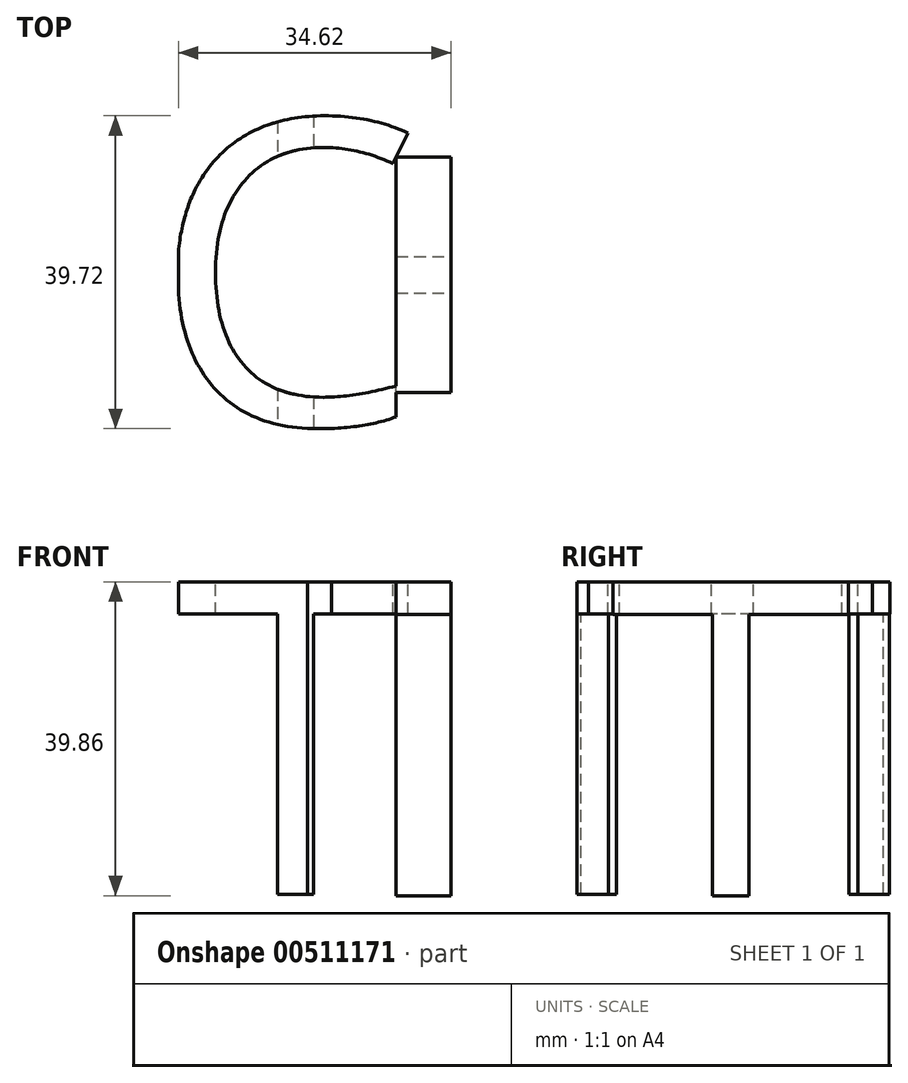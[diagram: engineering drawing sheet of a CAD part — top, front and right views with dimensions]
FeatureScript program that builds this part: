
annotation { "Feature Type Name" : "Feature", "Feature Type Description" : "" }
export const myFeature = defineFeature(function(context is Context, id is Id, definition is map)
    precondition{}
    {
        {
            var Q0;
            Q0=qCreatedBy(makeId("Top.planeOp"),FACE);
            var sketch = newSketch(context, id + "F0", { "sketchPlane" : qUnion([Q0])});
            skLineSegment(sketch, "E0.bottom", {"start": v(-20, 20) * mm, "end": v(20, 20) * mm});
            skLineSegment(sketch, "E0.top", {"start": v(-20, -20) * mm, "end": v(20, -20) * mm});
            skLineSegment(sketch, "E0.left", {"start": v(-20, 20) * mm, "end": v(-20, -20) * mm});
            skLineSegment(sketch, "E0.right", {"start": v(20, 20) * mm, "end": v(20, -20) * mm});
            skLineSegment(sketch, "E1", {"start": v(-20, 0) * mm, "end": v(20, 0) * mm, "construction": true});
            skSolve(sketch);
        }
        {
            var Q0;
            Q0 = qSketchRegion(id + "F0", true);
            extrude(context, id + "F1", {"entities" : qUnion([Q0]), "oppositeDirection" : true, "depth" : 40 * mm});
        }
        {
            var Q0;
            Q0=makeQuery(id+"F1.opExtrude","CAP_FACE",FACE,{"disambiguationData":[OSD([sQuery(id+"F0.wireOp",EDGE,"E0.bottom"),sQuery(id+"F0.wireOp",EDGE,"E0.top"),sQuery(id+"F0.wireOp",EDGE,"E0.left"),sQuery(id+"F0.wireOp",EDGE,"E0.right")])],"isStart":true});
            var sketch = newSketch(context, id + "F2", { "sketchPlane" : qUnion([Q0])});
            skText(sketch, "E2", { "text": "C\n", "fontName": "OpenSans-Regular.ttf"});
            const initialGuessF2  = {"E2": [-0.01804, -0.0195, 1, 0, 0.039]};
            skSetInitialGuess(sketch, initialGuessF2);
            skSolve(sketch);
        }
        {
            var Q0;
            Q0=makeQuery(id+"F1.opExtrude","SWEPT_FACE",FACE,{"disambiguationData":[OSD([sQuery(id+"F0.wireOp",EDGE,"E0.top")])]});
            var sketch = newSketch(context, id + "F3", { "sketchPlane" : qUnion([Q0])});
            skText(sketch, "E3", { "text": "T", "fontName": "OpenSans-Regular.ttf"});
            skLineSegment(sketch, "E4", {"start": v(-20, -20) * mm, "end": v(20, -20) * mm, "construction": true});
            const initialGuessF3  = {"E3": [-0.01511, -0.04, 1, 0, 0.04]};
            skSetInitialGuess(sketch, initialGuessF3);
            skSolve(sketch);
        }
        {
            var Q0;
            Q0=makeQuery(id+"F1.opExtrude","SWEPT_FACE",FACE,{"disambiguationData":[OSD([sQuery(id+"F0.wireOp",EDGE,"E0.right")])]});
            var sketch = newSketch(context, id + "F4", { "sketchPlane" : qUnion([Q0])});
            skText(sketch, "E5", { "text": "T", "fontName": "OpenSans-Regular.ttf"});
            skLineSegment(sketch, "E6", {"start": v(-20, -20) * mm, "end": v(20, -20) * mm, "construction": true});
            const initialGuessF4  = {"E5": [-0.0159, -0.0402, 1, 0, 0.0402]};
            skSetInitialGuess(sketch, initialGuessF4);
            skSolve(sketch);
        }
        {
            var Q0;
            Q0=makeQuery(id+"F2.imprint","IMPRINT",FACE,{"disambiguationData":[TD([[makeQuery(id+"F2.imprint","IMPRINT",EDGE,{"derivedFrom":sQuery(id+"F2.wireOp",EDGE,"E2.sketch_text.stroke-0")}),1.0]])]});
            extrude(context, id + "F5", {"entities" : qUnion([Q0]), "operationType" : NewBodyOperationType.REMOVE, "oppositeDirection" : true, "depth" : 40 * mm});
        }
        {
            var Q0;
            {var subQ4=sQuery(id+"F3.wireOp",EDGE,"E3.sketch_text.stroke-1");Q0=makeQuery(id+"F3.imprint","IMPRINT",FACE,{"disambiguationData":[TD([[makeQuery(id+"F3.imprint","IMPRINT",EDGE,{"derivedFrom":subQ4}),1.0]])]});}
            extrude(context, id + "F6", {"entities" : qUnion([Q0]), "operationType" : NewBodyOperationType.REMOVE, "oppositeDirection" : true, "depth" : 40 * mm});
        }
        {
            var Q0;
            Q0 = qSketchRegion(id + "F4", true);
            var Q1;
            Q1=makeQuery(id+"F5.boolean.opBoolean","COPY",FACE,{"derivedFrom":makeQuery(id+"F5.opExtrude","SWEPT_FACE",FACE,{"disambiguationData":[OSD([sQuery(id+"F2.wireOp",EDGE,"E2.sketch_text.stroke-5")])]})});
            extrude(context, id + "F7", {"entities" : qUnion([Q0]), "operationType" : NewBodyOperationType.ADD, "endBound" : BoundingType.UP_TO_SURFACE, "oppositeDirection" : true, "endBoundEntityFace" : qUnion([Q1]), "depth" : 25.4 * mm});
        }
    });
